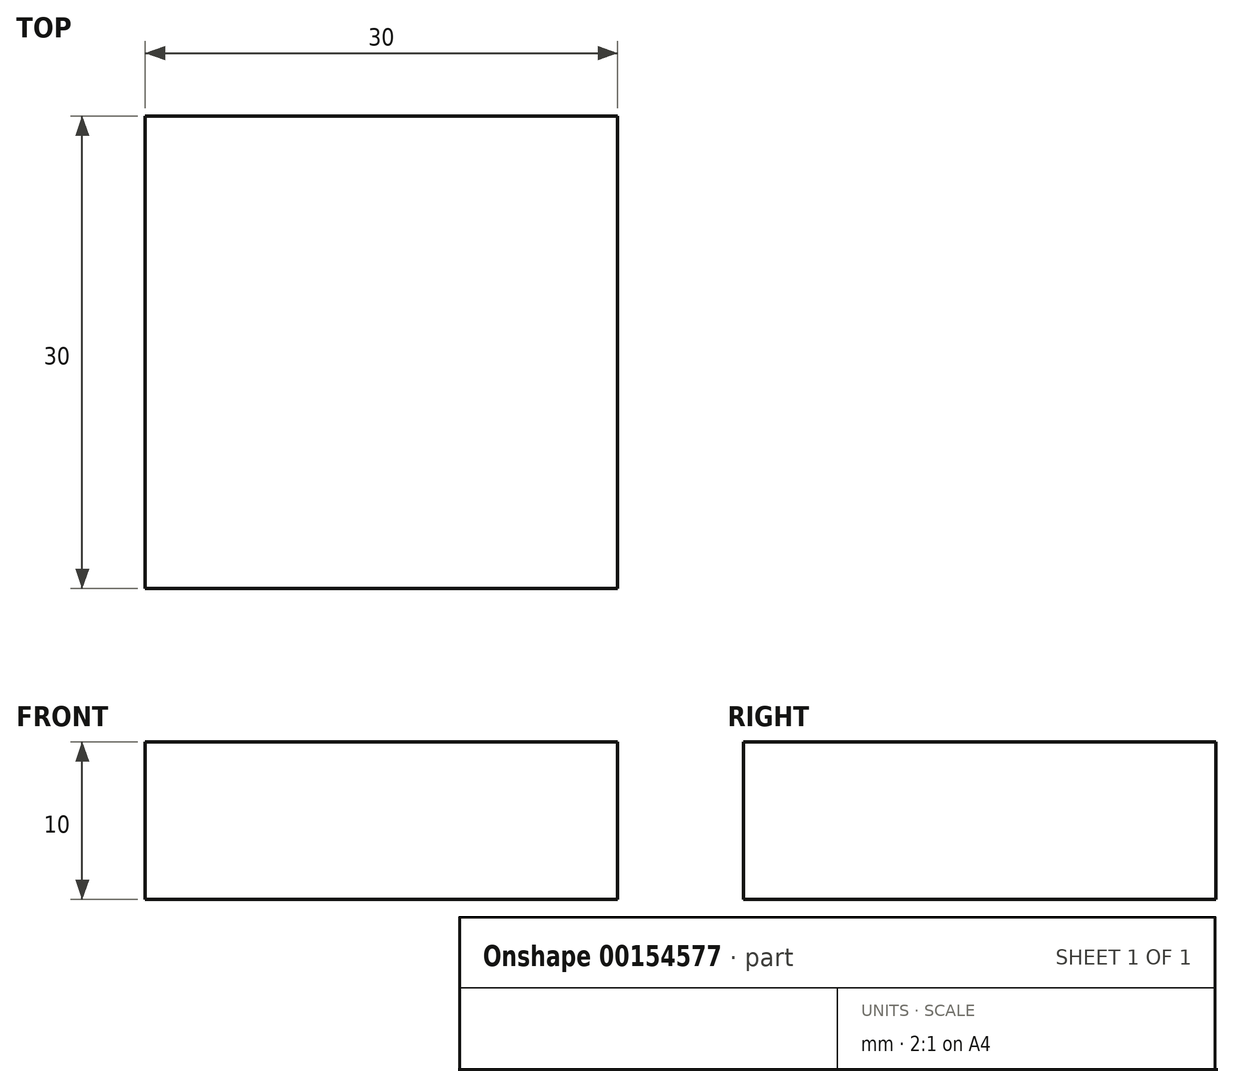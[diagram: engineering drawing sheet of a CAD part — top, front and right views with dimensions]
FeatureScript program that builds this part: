
annotation { "Feature Type Name" : "Feature", "Feature Type Description" : "" }
export const myFeature = defineFeature(function(context is Context, id is Id, definition is map)
    precondition{}
    {
        {
            var Q0;
            Q0=qCreatedBy(makeId("Top.planeOp"),FACE);
            var sketch = newSketch(context, id + "F0", { "sketchPlane" : qUnion([Q0])});
            skLineSegment(sketch, "E0.bottom", {"start": v(15, -15) * mm, "end": v(-15, -15) * mm});
            skLineSegment(sketch, "E0.top", {"start": v(15, 15) * mm, "end": v(-15, 15) * mm});
            skLineSegment(sketch, "E0.left", {"start": v(15, -15) * mm, "end": v(15, 15) * mm});
            skLineSegment(sketch, "E0.right", {"start": v(-15, -15) * mm, "end": v(-15, 15) * mm});
            skPoint(sketch, "E0.middle", {"position": v(0, 0) * mm});
            skSolve(sketch);
        }
        {
            var Q0;
            Q0 = qSketchRegion(id + "F0", true);
            extrude(context, id + "F1", {"entities" : qUnion([Q0]), "depth" : 10 * mm});
        }
    });
